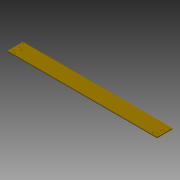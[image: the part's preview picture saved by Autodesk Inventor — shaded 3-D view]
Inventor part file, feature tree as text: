
AUTODESK INVENTOR PART (.ipt)
format: ipt  version: 2013 SP2 (Build 170200200, 200)  size: 112,640 bytes
history: native  units: mm
features: reference x8, extrude x2, sketch x1
ambient origin geometry x8: Origin, YZ Plane, XZ Plane, XY Plane, X Axis, Y Axis, Z Axis, Center Point
bodies: Solid1 (feature_tree)
feature tree (11):
  extrude  "Extrusion1"  Depth=3.0mm
  extrude  "Extrusion2"  Depth=486.0mm TaperAngle=0.0deg
  sketch  "Sketch1"  dims[d0=50.0mm d1=3.0mm d2=486.0mm d3=0.0mm d4=3.0mm d5=3.0mm d9=3.0mm d10=10.0mm d11=0.0mm d14=20.0mm d15=5.0mm d16=3.0mm d19=5.0mm d20=20.0mm d22=9.6mm d23=9.6mm d24=9.6mm d25=9.6mm d26=3.0mm d27=3.0mm d28=3.0mm d29=3.0mm d30=10.0mm d31=20.0mm]
  reference  "Reference1"
  reference  "Reference3"
  reference  "Reference4"
  reference  "Reference5"
  reference  "Reference7"
  reference  "Reference8"
  reference  "Reference9"
  reference  "Reference10"
